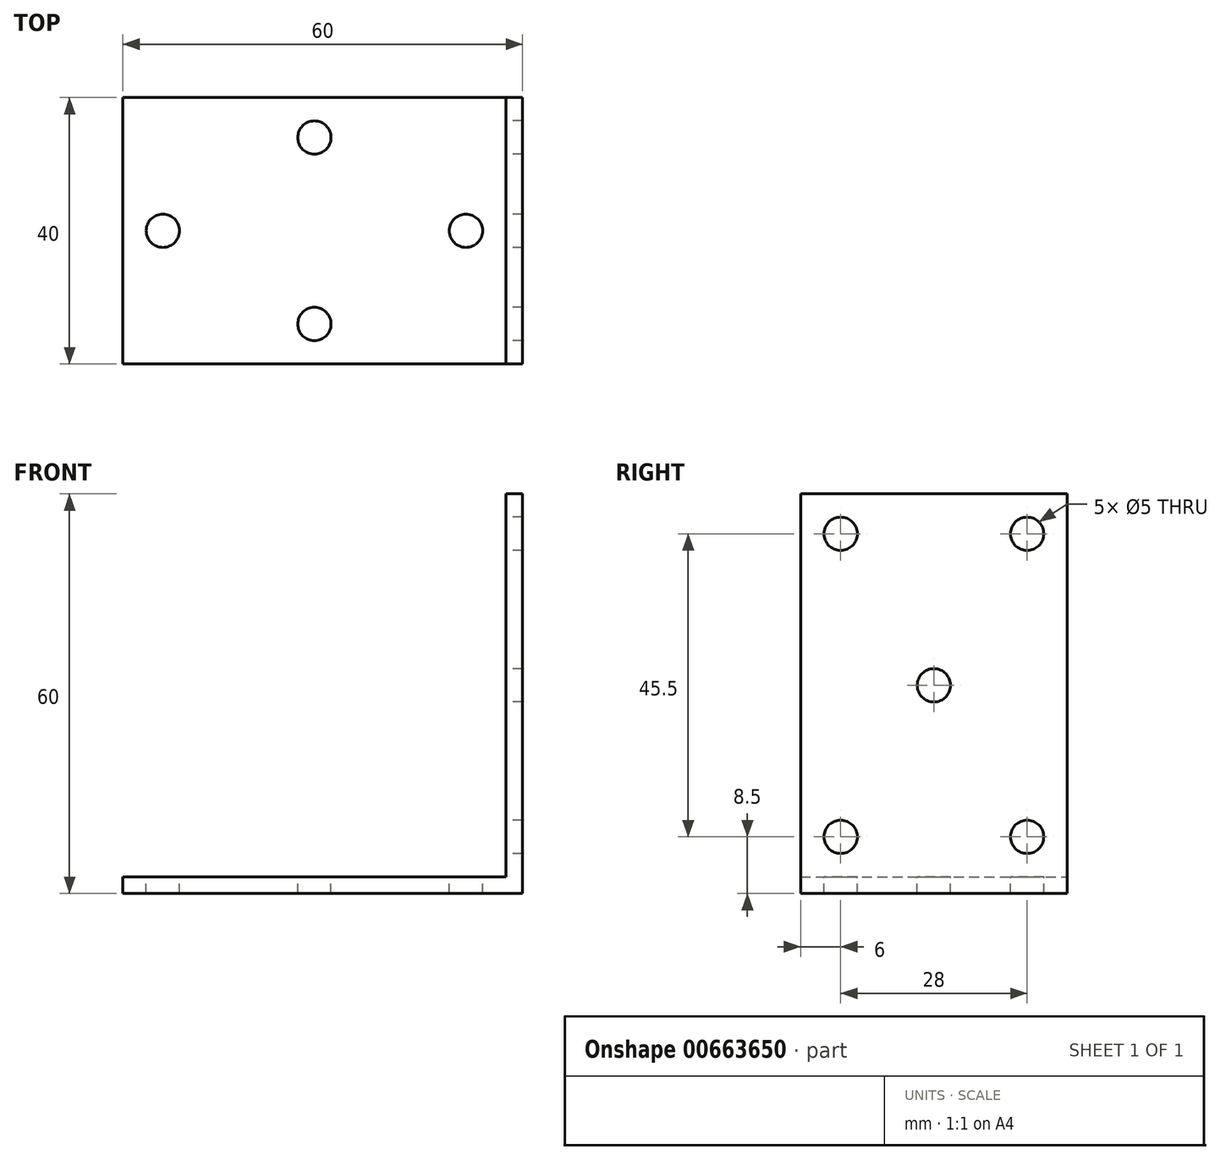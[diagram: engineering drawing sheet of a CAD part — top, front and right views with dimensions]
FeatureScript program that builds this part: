
annotation { "Feature Type Name" : "Feature", "Feature Type Description" : "" }
export const myFeature = defineFeature(function(context is Context, id is Id, definition is map)
    precondition{}
    {
        {
            var Q0;
            Q0=qCreatedBy(makeId("Front.planeOp"),FACE);
            var sketch = newSketch(context, id + "F0", { "sketchPlane" : qUnion([Q0])});
            skLineSegment(sketch, "E0", {"start": v(-60, 0) * mm, "end": v(0, 0) * mm});
            skLineSegment(sketch, "E1", {"start": v(0, 0) * mm, "end": v(0, 60) * mm});
            skLineSegment(sketch, "E2.0", {"start": v(-2.5, 2.5) * mm, "end": v(-2.5, 60) * mm});
            skLineSegment(sketch, "E2.1", {"start": v(-60, 2.5) * mm, "end": v(-2.5, 2.5) * mm});
            skLineSegment(sketch, "E3", {"start": v(-60, 2.5) * mm, "end": v(-60, 0) * mm});
            skLineSegment(sketch, "E4", {"start": v(-2.5, 60) * mm, "end": v(0, 60) * mm});
            skSolve(sketch);
        }
        {
            var Q0;
            Q0 = qSketchRegion(id + "F0", true);
            extrude(context, id + "F1", {"entities" : qUnion([Q0]), "depth" : 40 * mm, "offsetDistance" : 25 * mm, "symmetric" : true});
        }
        {
            var Q0;
            Q0=makeQuery(id+"F1.opExtrude","SWEPT_FACE",FACE,{"disambiguationData":[OSD([sQuery(id+"F0.wireOp",EDGE,"E2.0")])]});
            var sketch = newSketch(context, id + "F2", { "sketchPlane" : qUnion([Q0])});
            skLineSegment(sketch, "E5", {"start": v(0, 60) * mm, "end": v(0, 2.5) * mm, "construction": true});
            skCircle(sketch, "E6", {"center": v(0, 31.25) * mm, "radius": 2.5 * mm});
            skCircle(sketch, "E7", {"center": v(-14, 8.5) * mm, "radius": 2.5 * mm});
            skCircle(sketch, "E8", {"center": v(-14, 54) * mm, "radius": 2.5 * mm});
            skCircle(sketch, "E9.MirrorC", {"center": v(14, 54) * mm, "radius": 2.5 * mm});
            skCircle(sketch, "E10.MirrorC", {"center": v(14, 8.5) * mm, "radius": 2.5 * mm});
            skSolve(sketch);
        }
        {
            var Q0;
            Q0 = qSketchRegion(id + "F2", true);
            extrude(context, id + "F3", {"entities" : qUnion([Q0]), "operationType" : NewBodyOperationType.REMOVE, "oppositeDirection" : true, "depth" : 25 * mm, "offsetDistance" : 25 * mm});
        }
        {
            var Q0;
            Q0=makeQuery(id+"F1.opExtrude","SWEPT_FACE",FACE,{"disambiguationData":[OSD([sQuery(id+"F0.wireOp",EDGE,"E2.1")])]});
            var sketch = newSketch(context, id + "F4", { "sketchPlane" : qUnion([Q0])});
            skLineSegment(sketch, "E11", {"start": v(-60, 0) * mm, "end": v(-2.5, 0) * mm, "construction": true});
            skLineSegment(sketch, "E12", {"start": v(-31.25, 20) * mm, "end": v(-31.25, -20) * mm, "construction": true});
            skCircle(sketch, "E13", {"center": v(-54, 0) * mm, "radius": 2.5 * mm});
            skCircle(sketch, "E14", {"center": v(-31.25, 14) * mm, "radius": 2.5 * mm});
            skCircle(sketch, "E15.MirrorC", {"center": v(-31.25, -14) * mm, "radius": 2.5 * mm});
            skCircle(sketch, "E16.MirrorC", {"center": v(-8.5, 0) * mm, "radius": 2.5 * mm});
            skSolve(sketch);
        }
        {
            var Q0;
            Q0 = qSketchRegion(id + "F4", true);
            extrude(context, id + "F5", {"entities" : qUnion([Q0]), "operationType" : NewBodyOperationType.REMOVE, "oppositeDirection" : true, "depth" : 25 * mm, "offsetDistance" : 25 * mm});
        }
    });
